# Revit family: planox_672597_009_89_e8f9
name_source: partatom
category: Lighting Fixtures
units: mm (PartAtom-declared; Revit-internal decimal feet)

## family parameters
Cut with Voids When Loaded = No
Host = Face
Light Source = No
Part Type = Normal
Room Calculation Point = No
Round Connector Dimension = Use Diameter
Shared = No

## types (1)
- PLANOX (1 x LED Modul 840, 3100 lm, 4000)
    Apparent Load = 23 VA
    CIE Flux Codes = 42 72 91 92 100
    Color Rendering = 80
    Color Temperature = 4000
    Default Elevation = 1800 mm
    Description = Series: PLANOX
Classic moisture-proof diffuser luminaire with two-part luminaire design. For escape route illumination. Housing made of shockproof, UV-resistant plastic (polycarbonate). Injected silicone-based seal with increased resistance even under extreme conditions. Diffuser made of shockproof opal plastic (polycarbonate) with excellent light transmission of up to 90%. Diffuser fixed by stainless steel clips for easy installation and opening. Symmetrical light distribution. Homogeneous light distribution. Flexible and easy installation thanks to sliding quick-fix brackets made of stainless steel and diffuser with integrated gear tray as well as variable cable entry (face or rear sided). Suitable for Ceiling mounting, Suspension cable/chain, Wall (surface). Ceiling mounting stainless steel brackets and triangular brackets for pendant mounting included in delivery. Driver integrated. Suitable for connection to central battery systems. With AC Control monitoring module for LUXIFAIR central battery units. 
Colour: light grey (RAL 7035)
Length: 615 mm
Width: 102 mm
Height: 85 mm
Weight: 1.2 kg
Operating mode: maintained power mode
Lamp: LED
Socket: without socket
Colour temperature: 4000K
Colour rendering index (CRI): 80
System power: 23 W
Rated luminous flux: 3100 lm
Luminous flux, emergency: 800 lm
System power, emergency: 9 W
Control gear: Regulated power supply
Protection class: I
Type of protection: IP 66
    Height = 85 mm
    Lamp = 1 x LED Modul 840
    Lamp Light Flux = 3100 lm
    Lamp count = 1
    Length = 615 mm
    Lifetime = 50000 h
    Luminous efficacy = 135 lm/W
    Manufacturer = RZB
    ModVariant = No
    Model = 672597.009.89
    Mounting Place = Ceiling
    Mounting Type = Surface mounted
    Number of Poles = 1
    OnlyDefault = Yes
    Power Factor = 1
    Product Name = PLANOX
    Product group = Surface mounted ceiling and wall luminaires
    ProductGroupID = 305
    Protection Class = Protection class I
    Protection Degree = Degree of protection
    RLX_Detail_Level = 1
    RLX_Emergency_Light_Flux = 0 lm
    RLX_Emergency_Type = 0
    RLX_Emergency_Type_DB = No
    RlxData = <blob elided: 49181 chars, md5=d4c8448d>
    Socket = socket
    Standby Power = 0 W
    System Light Flux = 3100 lm
    System Power = 23 W
    Type Comments = ALEA SPOT
    Type Image = 451230.009.jpg
    URL = http://relux.com
    VarID = ---
    Voltage = 0 V
    Weight = 0.00 kg
    Width = 102 mm

## geometry (parser evidence)
native form markers: Sweep x13
no freeform markers — native parametric forms only
